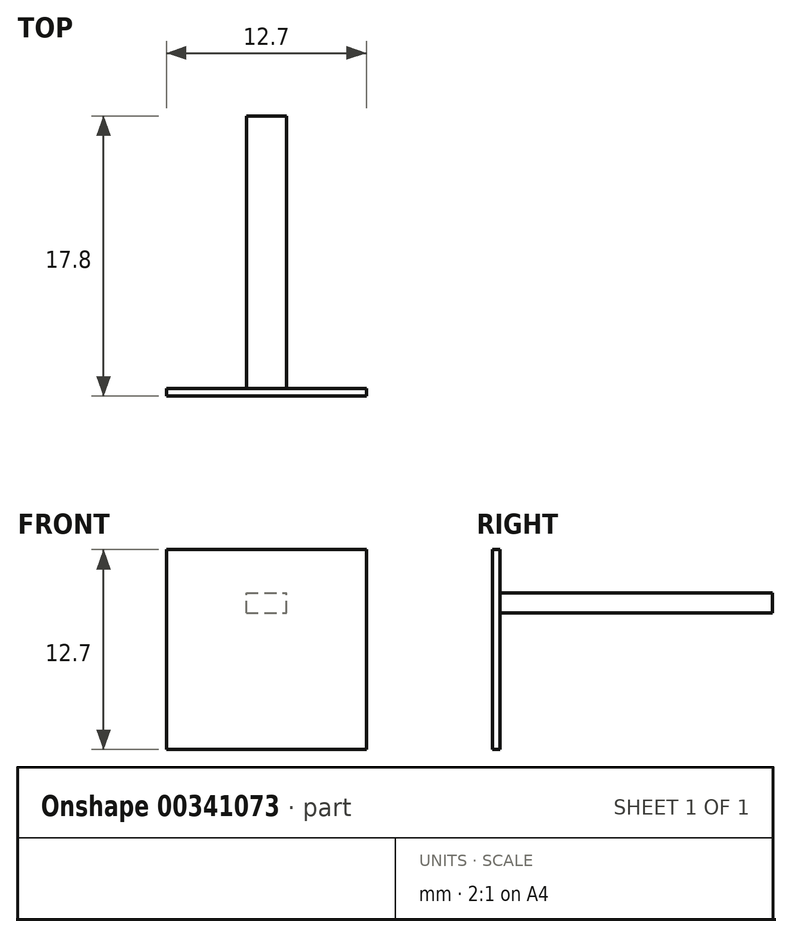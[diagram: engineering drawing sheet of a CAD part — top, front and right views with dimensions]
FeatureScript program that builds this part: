
annotation { "Feature Type Name" : "Feature", "Feature Type Description" : "" }
export const myFeature = defineFeature(function(context is Context, id is Id, definition is map)
    precondition{}
    {
        {
            assignVariable(context, id + "F0", {"name" : "L", "anyValue" : .5});
        }
        {
            var Q0;
            Q0=qCreatedBy(makeId("Front.planeOp"),FACE);
            var sketch = newSketch(context, id + "F1", { "sketchPlane" : qUnion([Q0])});
            skLineSegment(sketch, "E0.bottom", {"start": v(6.35, -6.35) * mm, "end": v(-6.35, -6.35) * mm});
            skLineSegment(sketch, "E0.top", {"start": v(6.35, 6.35) * mm, "end": v(-6.35, 6.35) * mm});
            skLineSegment(sketch, "E0.left", {"start": v(6.35, -6.35) * mm, "end": v(6.35, 6.35) * mm});
            skLineSegment(sketch, "E0.right", {"start": v(-6.35, -6.35) * mm, "end": v(-6.35, 6.35) * mm});
            skPoint(sketch, "E0.middle", {"position": v(0, 0) * mm});
            skSolve(sketch);
        }
        {
            var Q0;
            Q0 = qSketchRegion(id + "F1", true);
            extrude(context, id + "F2", {"entities" : qUnion([Q0]), "depth" : (getVariable(context, 'L')) * mm, "symmetric" : true});
        }
        {
            var Q0;
            Q0=qCreatedBy(makeId("Right.planeOp"),FACE);
            var sketch = newSketch(context, id + "F3", { "sketchPlane" : qUnion([Q0])});
            skLineSegment(sketch, "E1", {"start": v(6.35, 2.97) * mm, "end": v(23.65, 2.97) * mm});
            skLineSegment(sketch, "E2.0", {"start": v(6.35, -6.35) * mm, "end": v(6.35, 6.35) * mm});
            skSolve(sketch);
        }
        {
            var Q0;
            Q0=makeQuery(id+"F2.opExtrude","CAP_FACE",FACE,{"disambiguationData":[OSD([sQuery(id+"F1.wireOp",EDGE,"E0.bottom"),sQuery(id+"F1.wireOp",EDGE,"E0.top"),sQuery(id+"F1.wireOp",EDGE,"E0.left"),sQuery(id+"F1.wireOp",EDGE,"E0.right")])],"isStart":true});
            var sketch = newSketch(context, id + "F4", { "sketchPlane" : qUnion([Q0])});
            skPoint(sketch, "E3.0", {"position": v(0, 2.97) * mm});
            skLineSegment(sketch, "E4.bottom", {"start": v(1.27, 2.34) * mm, "end": v(-1.27, 2.34) * mm});
            skLineSegment(sketch, "E4.top", {"start": v(1.27, 3.6) * mm, "end": v(-1.27, 3.6) * mm});
            skLineSegment(sketch, "E4.left", {"start": v(1.27, 2.34) * mm, "end": v(1.27, 3.6) * mm});
            skLineSegment(sketch, "E4.right", {"start": v(-1.27, 2.34) * mm, "end": v(-1.27, 3.6) * mm});
            skSolve(sketch);
        }
        {
            var Q0;
            Q0=makeQuery(id+"F4.imprint","IMPRINT",FACE,{"disambiguationData":[TD([[makeQuery(id+"F4.imprint","IMPRINT",EDGE,{"derivedFrom":sQuery(id+"F4.wireOp",EDGE,"E4.bottom")}),-1.0]])]});
            var Q1;
            Q1=sQuery(id+"F3.wireOp",EDGE,"E1");
            sweep(context, id + "F5", {"profiles" : qUnion([Q0]), "path" : qUnion([Q1])});
        }
    });
